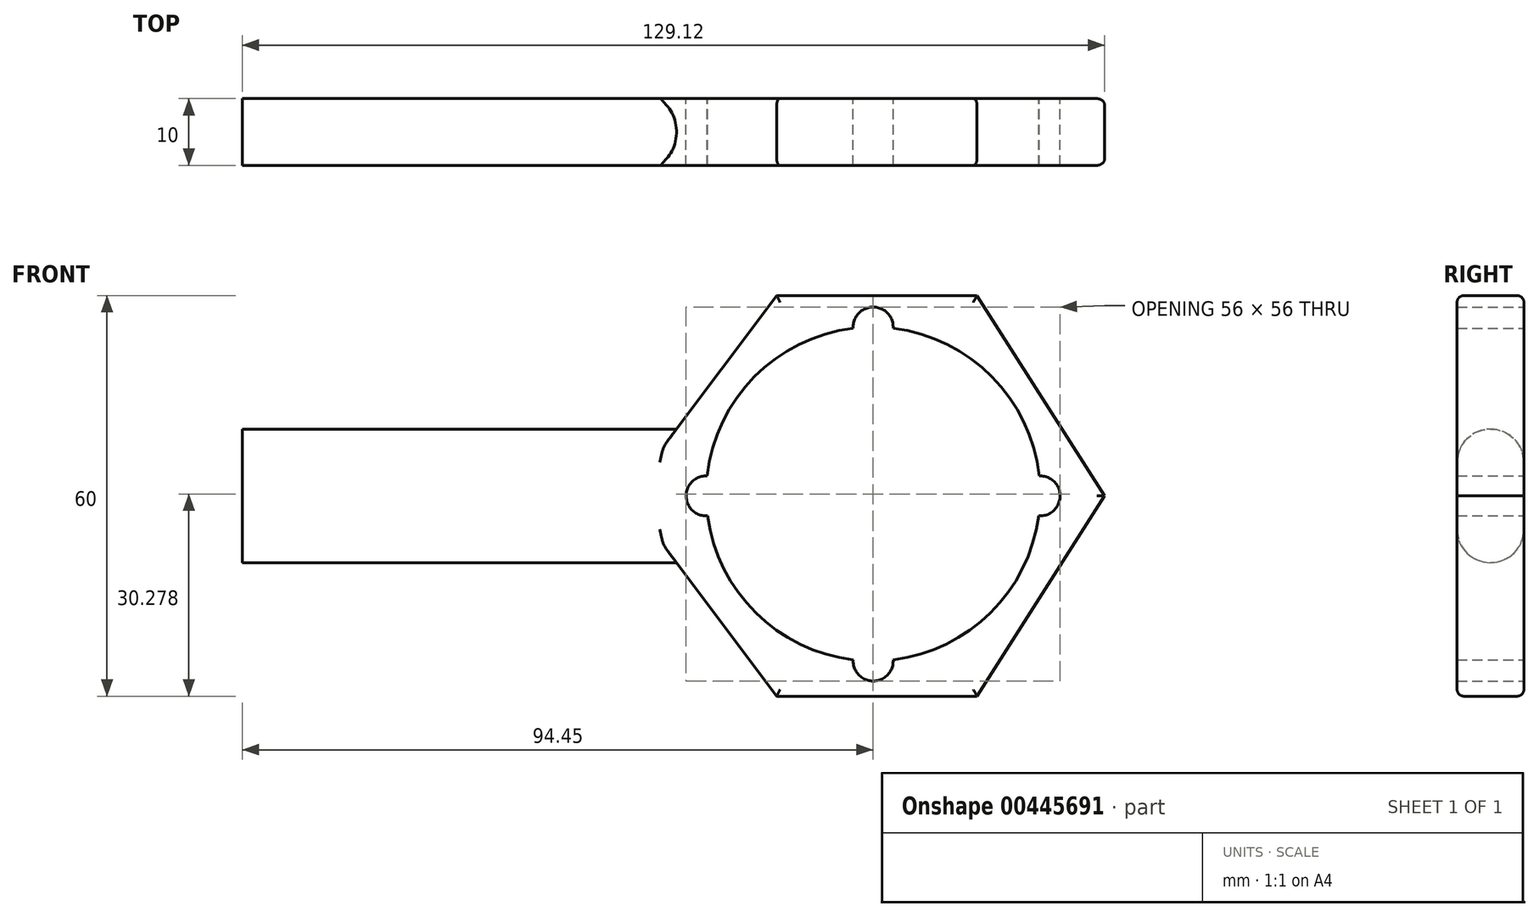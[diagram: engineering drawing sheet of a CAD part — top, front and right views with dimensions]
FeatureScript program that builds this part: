
annotation { "Feature Type Name" : "Feature", "Feature Type Description" : "" }
export const myFeature = defineFeature(function(context is Context, id is Id, definition is map)
    precondition{}
    {
        {
            var Q0;
            Q0=qCreatedBy(makeId("Front.planeOp"),FACE);
            var sketch = newSketch(context, id + "F0", { "sketchPlane" : qUnion([Q0])});
            skLineSegment(sketch, "E0.0", {"start": v(15.55, -30) * mm, "end": v(45.55, -30) * mm});
            skLineSegment(sketch, "E1.0", {"start": v(15.55, 30) * mm, "end": v(45.55, 30) * mm});
            skLineSegment(sketch, "E2", {"start": v(-64.45, 30) * mm, "end": v(-64.45, 30) * mm});
            skLineSegment(sketch, "E3", {"start": v(-64.45, 10) * mm, "end": v(-64.45, -10) * mm});
            skCircle(sketch, "E4", {"center": v(30, 0.28) * mm, "radius": 0.28 * mm});
            skArc(sketch, "E5", {"start": v(54.85, 3) * mm, "mid": v(47.78, 17.86) * mm, "end": v(33, 25.1) * mm});
            skArc(sketch, "E6", {"start": v(33, 25.1) * mm, "mid": v(30, 28.28) * mm, "end": v(27, 25.1) * mm});
            skArc(sketch, "E7", {"start": v(27, -24.54) * mm, "mid": v(30, -27.72) * mm, "end": v(33, -24.54) * mm});
            skArc(sketch, "E8", {"start": v(5.15, 3) * mm, "mid": v(2, -0.03) * mm, "end": v(5.21, -3) * mm});
            skArc(sketch, "E9", {"start": v(54.79, -3) * mm, "mid": v(58, -0.03) * mm, "end": v(54.85, 3) * mm});
            skArc(sketch, "E10.trimOffspring", {"start": v(33, -24.54) * mm, "mid": v(47.58, -17.5) * mm, "end": v(54.79, -3) * mm});
            skArc(sketch, "E11.trimOffspring", {"start": v(5.21, -3) * mm, "mid": v(12.42, -17.5) * mm, "end": v(27, -24.54) * mm});
            skArc(sketch, "E12.trimOffspring", {"start": v(27, 25.1) * mm, "mid": v(12.22, 17.86) * mm, "end": v(5.15, 3) * mm});
            skLineSegment(sketch, "E13.trimOffspring", {"start": v(30, 0) * mm, "end": v(30, 0.56) * mm});
            skLineSegment(sketch, "E14.0", {"start": v(-64.45, -10) * mm, "end": v(0.55, -10) * mm});
            skLineSegment(sketch, "E15.0", {"start": v(-64.45, 10) * mm, "end": v(0.55, 10) * mm});
            skLineSegment(sketch, "E16", {"start": v(0.55, 10) * mm, "end": v(15.55, 30) * mm});
            skLineSegment(sketch, "E17", {"start": v(0.55, -10) * mm, "end": v(15.55, -30) * mm});
            skLineSegment(sketch, "E18", {"start": v(64.67, 0) * mm, "end": v(45.55, 30) * mm});
            skLineSegment(sketch, "E19", {"start": v(64.67, 0) * mm, "end": v(45.55, -30) * mm});
            skPoint(sketch, "E20.orphan", {"position": v(30, 67.2) * mm});
            skPoint(sketch, "E21.start.orphan", {"position": v(0, -66.64) * mm});
            skPoint(sketch, "E22.0.start.orphan", {"position": v(30, -66.64) * mm});
            skPoint(sketch, "E23.orphan", {"position": v(-64.45, 0) * mm});
            skSolve(sketch);
        }
        {
            var Q0;
            Q0 = qSketchRegion(id + "F0", true);
            extrude(context, id + "F1", {"entities" : qUnion([Q0]), "depth" : 10 * mm});
        }
        {
            var Q0;
            Q0=makeQuery(id+"F1.opExtrude","CAP_EDGE",EDGE,{"disambiguationData":[OSD([sQuery(id+"F0.wireOp",EDGE,"E14.0")])],"isStart":false});
            var Q1;
            Q1=makeQuery(id+"F1.opExtrude","CAP_EDGE",EDGE,{"disambiguationData":[OSD([sQuery(id+"F0.wireOp",EDGE,"E14.0")])],"isStart":true});
            fillet(context, id + "F2", {"entities" : qUnion([Q0, Q1]), "radius" : 5 * mm, "tangentPropagation" : true, "allowEdgeOverflow" : false});
        }
        {
            var Q0;
            Q0=makeQuery(id+"F1.opExtrude","CAP_EDGE",EDGE,{"disambiguationData":[OSD([sQuery(id+"F0.wireOp",EDGE,"E15.0")])],"isStart":true});
            var Q1;
            Q1=makeQuery(id+"F1.opExtrude","CAP_EDGE",EDGE,{"disambiguationData":[OSD([sQuery(id+"F0.wireOp",EDGE,"E15.0")])],"isStart":false});
            fillet(context, id + "F3", {"entities" : qUnion([Q0, Q1]), "radius" : 5 * mm, "tangentPropagation" : true, "allowEdgeOverflow" : false});
        }
        {
            var Q0;
            Q0=makeQuery(id+"F1.opExtrude","CAP_EDGE",EDGE,{"disambiguationData":[OSD([sQuery(id+"F0.wireOp",EDGE,"E16")])],"isStart":false});
            var Q1;
            Q1=makeQuery(id+"F1.opExtrude","CAP_EDGE",EDGE,{"disambiguationData":[OSD([sQuery(id+"F0.wireOp",EDGE,"E1.0")])],"isStart":false});
            var Q2;
            Q2=makeQuery(id+"F1.opExtrude","CAP_EDGE",EDGE,{"disambiguationData":[OSD([sQuery(id+"F0.wireOp",EDGE,"E18")])],"isStart":false});
            var Q3;
            Q3=makeQuery(id+"F1.opExtrude","CAP_EDGE",EDGE,{"disambiguationData":[OSD([sQuery(id+"F0.wireOp",EDGE,"E19")])],"isStart":false});
            var Q4;
            Q4=makeQuery(id+"F1.opExtrude","CAP_EDGE",EDGE,{"disambiguationData":[OSD([sQuery(id+"F0.wireOp",EDGE,"E0.0")])],"isStart":false});
            var Q5;
            Q5=makeQuery(id+"F1.opExtrude","CAP_EDGE",EDGE,{"disambiguationData":[OSD([sQuery(id+"F0.wireOp",EDGE,"E17")])],"isStart":false});
            fillet(context, id + "F4", {"entities" : qUnion([Q0, Q1, Q2, Q3, Q4, Q5]), "radius" : 1 * mm, "tangentPropagation" : true, "allowEdgeOverflow" : false});
        }
        {
            var Q0;
            Q0=makeQuery(id+"F1.opExtrude","CAP_EDGE",EDGE,{"disambiguationData":[OSD([sQuery(id+"F0.wireOp",EDGE,"E1.0")])],"isStart":true});
            var Q1;
            Q1=makeQuery(id+"F1.opExtrude","CAP_EDGE",EDGE,{"disambiguationData":[OSD([sQuery(id+"F0.wireOp",EDGE,"E18")])],"isStart":true});
            var Q2;
            Q2=makeQuery(id+"F1.opExtrude","CAP_EDGE",EDGE,{"disambiguationData":[OSD([sQuery(id+"F0.wireOp",EDGE,"E19")])],"isStart":true});
            var Q3;
            Q3=makeQuery(id+"F1.opExtrude","CAP_EDGE",EDGE,{"disambiguationData":[OSD([sQuery(id+"F0.wireOp",EDGE,"E0.0")])],"isStart":true});
            var Q4;
            Q4=makeQuery(id+"F1.opExtrude","CAP_EDGE",EDGE,{"disambiguationData":[OSD([sQuery(id+"F0.wireOp",EDGE,"E17")])],"isStart":true});
            var Q5;
            Q5=makeQuery(id+"F1.opExtrude","CAP_EDGE",EDGE,{"disambiguationData":[OSD([sQuery(id+"F0.wireOp",EDGE,"E16")])],"isStart":true});
            fillet(context, id + "F5", {"entities" : qUnion([Q0, Q1, Q2, Q3, Q4, Q5]), "radius" : 1 * mm, "tangentPropagation" : true, "allowEdgeOverflow" : false});
        }
    });
